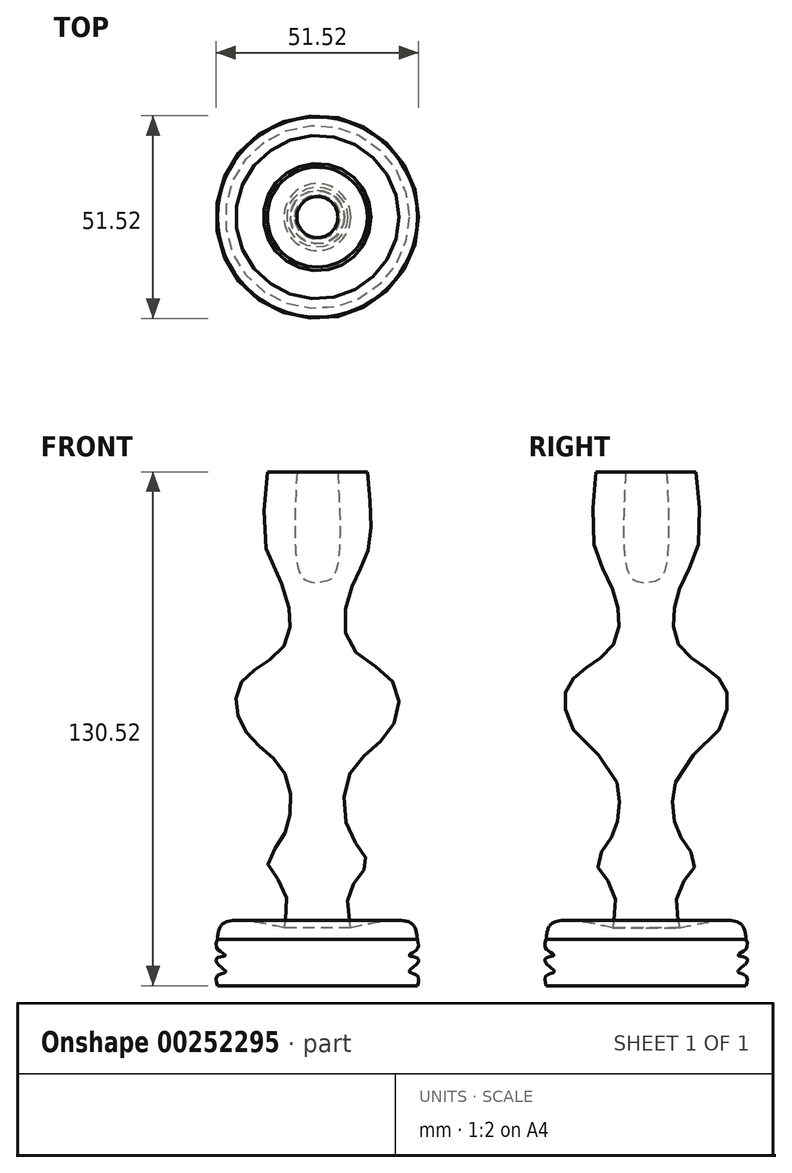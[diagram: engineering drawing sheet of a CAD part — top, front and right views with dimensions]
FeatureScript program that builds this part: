
annotation { "Feature Type Name" : "Feature", "Feature Type Description" : "" }
export const myFeature = defineFeature(function(context is Context, id is Id, definition is map)
    precondition{}
    {
        {
            var Q0;
            Q0=qCreatedBy(makeId("Front.planeOp"),FACE);
            var sketch = newSketch(context, id + "F0", { "sketchPlane" : qUnion([Q0])});
            skLineSegment(sketch, "E0", {"start": v(0, 110) * mm, "end": v(0, -112.58) * mm, "construction": true});
            skLineSegment(sketch, "E1", {"start": v(-5.2, 62) * mm, "end": v(-12.7, 62) * mm});
            skLineSegment(sketch, "E2", {"start": v(0, -68.52) * mm, "end": v(-25.4, -68.52) * mm});
            skFitSpline(sketch, "E3", {"points": [v(-25.4, -68.52) * mm, v(-25.4, -66) * mm, v(-23.31, -64.97) * mm, v(-25.4, -62.9) * mm, v(-25.4, -61.46) * mm, v(-23.31, -60.84) * mm, v(-25.4, -59.19) * mm, v(-25.4, -56.71) * mm], "startDerivative": vector(-6.07, 19.98) * mm, "endDerivative": vector(6, 17.8) * mm});
            skFitSpline(sketch, "E4", {"points": [v(-25.4, -56.71) * mm, v(-23.72, -52.58) * mm, v(-8.5, -53.82) * mm], "startDerivative": vector(1.5, 14.17) * mm, "endDerivative": vector(29.5, -6.35) * mm});
            skFitSpline(sketch, "E5", {"points": [v(-8.5, -53.82) * mm, v(-8.5, -43.7) * mm, v(-12.61, -37.3) * mm, v(-8.5, -30.29) * mm, v(-8.5, -14.19) * mm, v(-17.96, -4.28) * mm, v(-19.6, 8.11) * mm, v(-8.5, 17.81) * mm, v(-8.5, 32.26) * mm, v(-13.03, 42.59) * mm, v(-12.7, 62) * mm], "startDerivative": vector(23.2, 120.6) * mm, "endDerivative": vector(18.76, 173.48) * mm});
            skFitSpline(sketch, "E6", {"points": [v(-5.2, 62) * mm, v(-5.62, 43.2) * mm, v(-3.56, 34.95) * mm, v(0, 33.92) * mm], "startDerivative": vector(-2.2, -42.17) * mm, "endDerivative": vector(18.89, -1.05) * mm});
            skPoint(sketch, "E7.orphan", {"position": v(-25.4, 62) * mm});
            skLineSegment(sketch, "E8", {"start": v(0, 33.92) * mm, "end": v(0, -68.52) * mm});
            skPoint(sketch, "E9.orphan", {"position": v(0, 62) * mm});
            skSolve(sketch);
        }
        {
            var Q0;
            Q0=makeQuery(id+"F0.imprint","IMPRINT",FACE,{"disambiguationData":[TD([[makeQuery(id+"F0.imprint","IMPRINT",EDGE,{"derivedFrom":sQuery(id+"F0.wireOp",EDGE,"E1")}),1.0]])]});
            var Q1;
            Q1=sQuery(id+"F0.wireOp",EDGE,"E0");
            revolve(context, id + "F1", {"entities" : qUnion([Q0]), "axis" : qUnion([Q1]), "revolveType" : RevolveType.FULL});
        }
    });
